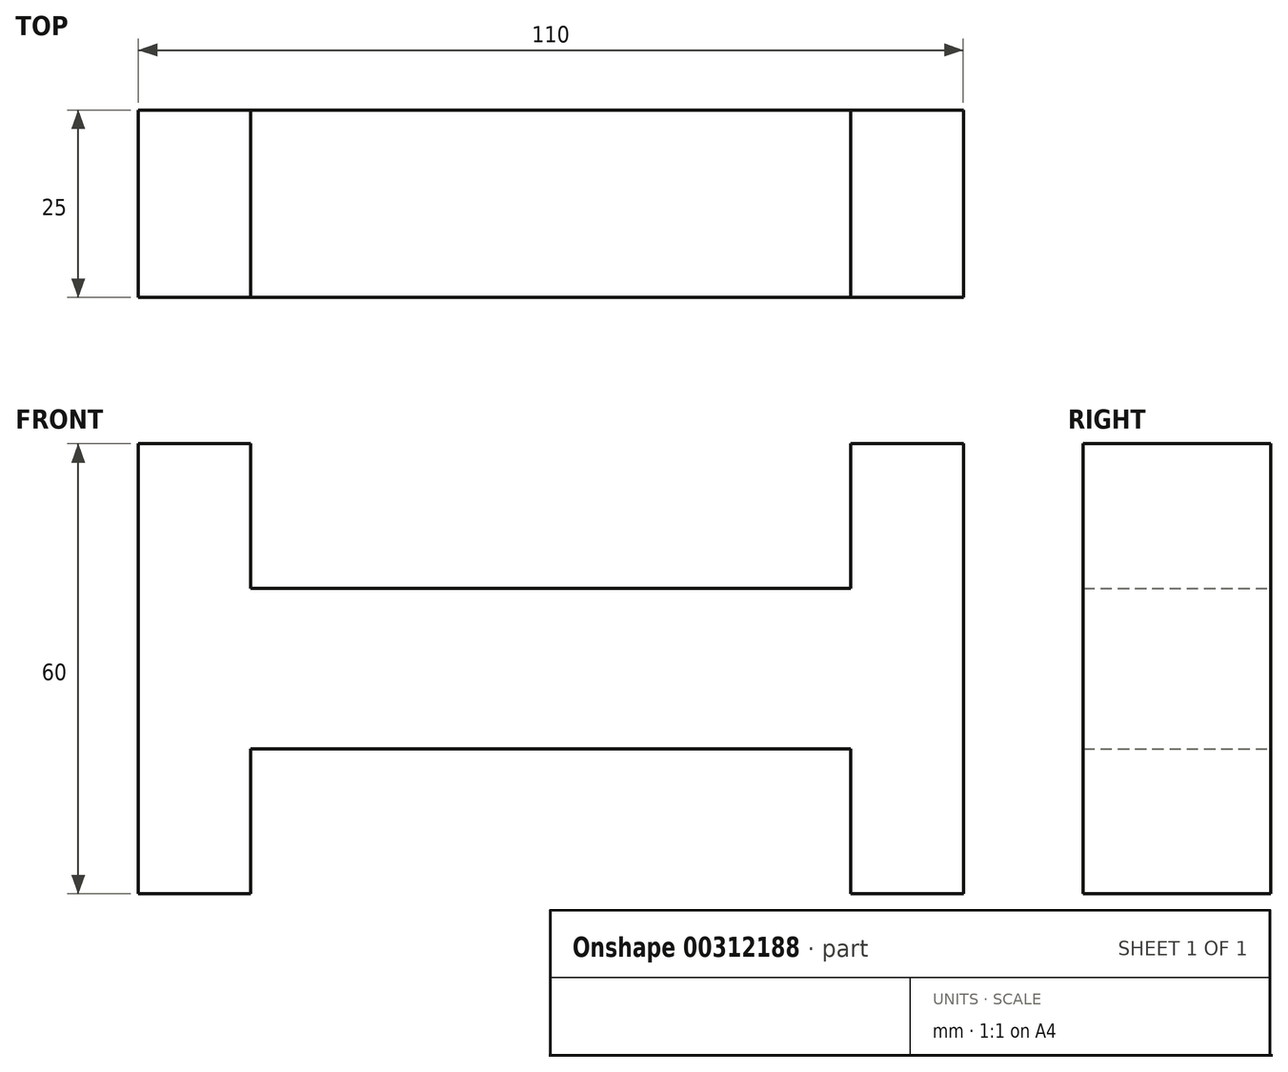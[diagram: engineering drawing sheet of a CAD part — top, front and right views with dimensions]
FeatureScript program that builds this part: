
annotation { "Feature Type Name" : "Feature", "Feature Type Description" : "" }
export const myFeature = defineFeature(function(context is Context, id is Id, definition is map)
    precondition{}
    {
        {
            var Q0;
            Q0=qCreatedBy(makeId("Front.planeOp"),FACE);
            var sketch = newSketch(context, id + "F0", { "sketchPlane" : qUnion([Q0])});
            skLineSegment(sketch, "E0", {"start": v(-34.15, -41.88) * mm, "end": v(-34.15, 18.12) * mm});
            skLineSegment(sketch, "E1", {"start": v(-34.15, 18.12) * mm, "end": v(-19.15, 18.12) * mm});
            skLineSegment(sketch, "E2", {"start": v(-19.15, 18.12) * mm, "end": v(-19.15, -1.18) * mm});
            skLineSegment(sketch, "E3", {"start": v(-19.15, -1.18) * mm, "end": v(60.85, -1.18) * mm});
            skLineSegment(sketch, "E4", {"start": v(60.85, -1.18) * mm, "end": v(60.85, 18.12) * mm});
            skLineSegment(sketch, "E5", {"start": v(60.85, 18.12) * mm, "end": v(75.85, 18.12) * mm});
            skLineSegment(sketch, "E6", {"start": v(75.85, 18.12) * mm, "end": v(75.85, -41.88) * mm});
            skLineSegment(sketch, "E7", {"start": v(75.85, -41.88) * mm, "end": v(60.85, -41.88) * mm});
            skLineSegment(sketch, "E8", {"start": v(60.85, -41.88) * mm, "end": v(60.85, -22.57) * mm});
            skLineSegment(sketch, "E9", {"start": v(60.85, -22.57) * mm, "end": v(-19.15, -22.57) * mm});
            skLineSegment(sketch, "E10", {"start": v(-19.15, -22.57) * mm, "end": v(-19.15, -41.88) * mm});
            skLineSegment(sketch, "E11", {"start": v(-19.15, -41.88) * mm, "end": v(-34.15, -41.88) * mm});
            skSolve(sketch);
        }
        {
            var Q0;
            Q0 = qSketchRegion(id + "F0", true);
            extrude(context, id + "F1", {"entities" : qUnion([Q0]), "depth" : 25 * mm});
        }
    });
